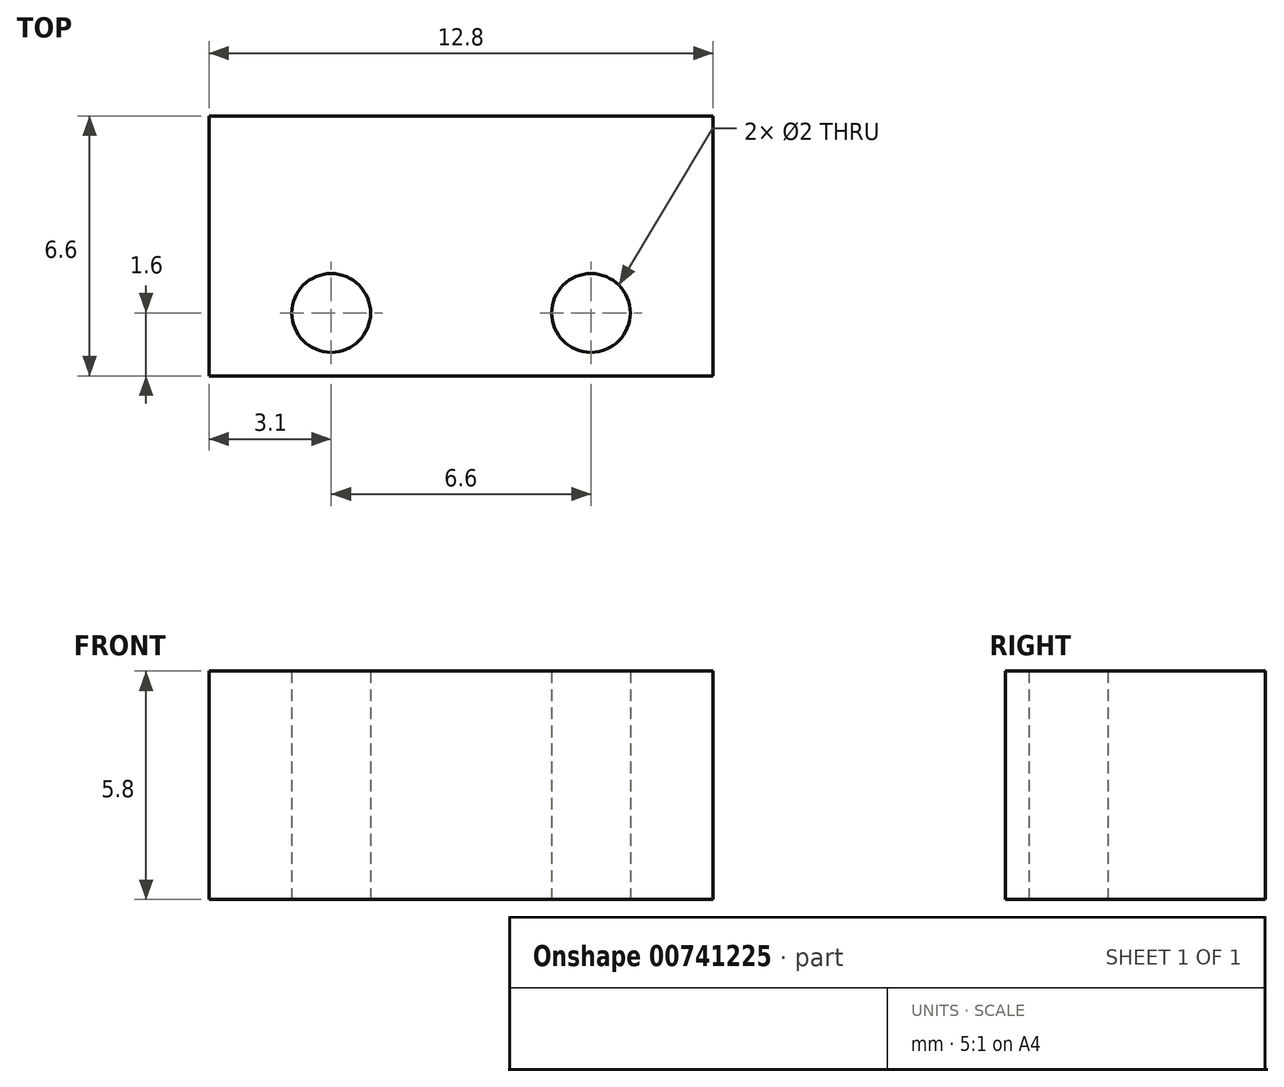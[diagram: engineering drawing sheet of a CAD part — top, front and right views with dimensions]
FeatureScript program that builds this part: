
annotation { "Feature Type Name" : "Feature", "Feature Type Description" : "" }
export const myFeature = defineFeature(function(context is Context, id is Id, definition is map)
    precondition{}
    {
        {
            var Q0;
            Q0=qCreatedBy(makeId("Top.planeOp"),FACE);
            var sketch = newSketch(context, id + "F0", { "sketchPlane" : qUnion([Q0])});
            skLineSegment(sketch, "E0.bottom", {"start": v(-6.4, 0) * mm, "end": v(6.4, 0) * mm});
            skLineSegment(sketch, "E0.top", {"start": v(-6.4, 6.6) * mm, "end": v(6.4, 6.6) * mm});
            skLineSegment(sketch, "E0.left", {"start": v(-6.4, 0) * mm, "end": v(-6.4, 6.6) * mm});
            skLineSegment(sketch, "E0.right", {"start": v(6.4, 0) * mm, "end": v(6.4, 6.6) * mm});
            skLineSegment(sketch, "E1", {"start": v(0, 0) * mm, "end": v(0, 7.49) * mm, "construction": true});
            skCircle(sketch, "E2", {"center": v(-3.3, 1.6) * mm, "radius": 1 * mm});
            skCircle(sketch, "E3.MirrorC", {"center": v(3.3, 1.6) * mm, "radius": 1 * mm});
            skSolve(sketch);
        }
        {
            var Q0;
            Q0=makeQuery(id+"F0.imprint","IMPRINT",FACE,{"disambiguationData":[TD([[makeQuery(id+"F0.imprint","IMPRINT",EDGE,{"derivedFrom":sQuery(id+"F0.wireOp",EDGE,"E0.bottom")}),1.0]])]});
            extrude(context, id + "F1", {"entities" : qUnion([Q0]), "depth" : 5.8 * mm, "offsetDistance" : 25 * mm});
        }
    });
